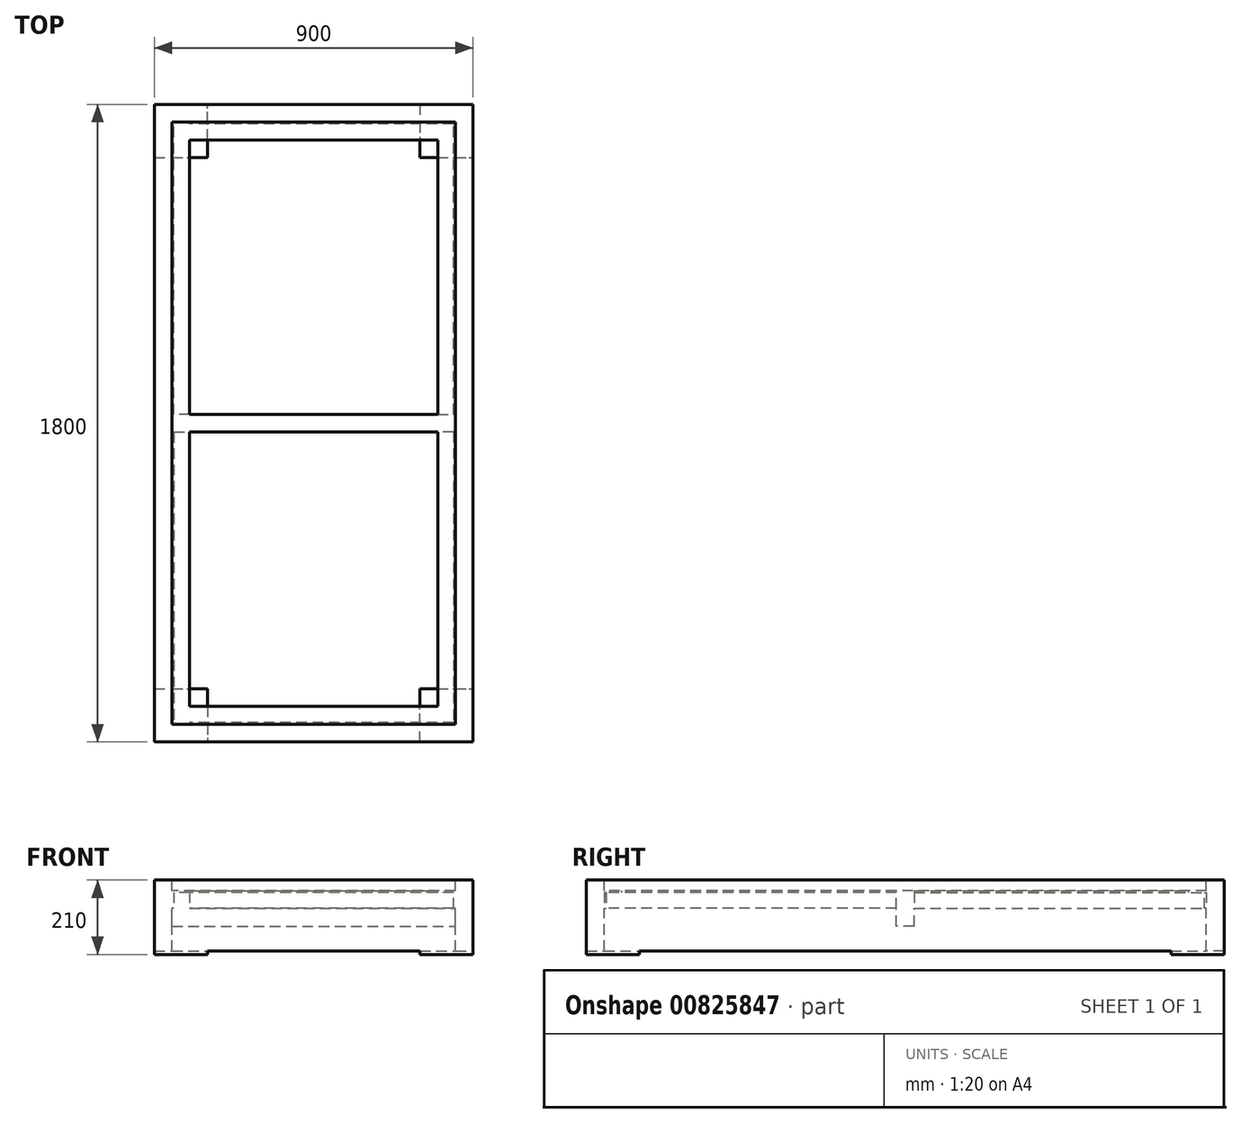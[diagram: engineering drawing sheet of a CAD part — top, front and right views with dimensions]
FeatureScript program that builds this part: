
annotation { "Feature Type Name" : "Feature", "Feature Type Description" : "" }
export const myFeature = defineFeature(function(context is Context, id is Id, definition is map)
    precondition{}
    {
        {
            var Q0;
            Q0=qCreatedBy(makeId("Top.planeOp"),FACE);
            var sketch = newSketch(context, id + "F0", { "sketchPlane" : qUnion([Q0])});
            skLineSegment(sketch, "E0", {"start": v(0, 0) * mm, "end": v(0, 1800) * mm});
            skLineSegment(sketch, "E1", {"start": v(0, 1800) * mm, "end": v(900, 1800) * mm});
            skLineSegment(sketch, "E2", {"start": v(900, 1800) * mm, "end": v(900, 0) * mm});
            skLineSegment(sketch, "E3", {"start": v(900, 0) * mm, "end": v(0, 0) * mm});
            skLineSegment(sketch, "E4.0", {"start": v(50, 50) * mm, "end": v(50, 1750) * mm});
            skLineSegment(sketch, "E5.0", {"start": v(50, 1750) * mm, "end": v(850, 1750) * mm});
            skLineSegment(sketch, "E6.0", {"start": v(850, 1750) * mm, "end": v(850, 50) * mm});
            skLineSegment(sketch, "E7.0", {"start": v(850, 50) * mm, "end": v(50, 50) * mm});
            skLineSegment(sketch, "E8.0", {"start": v(50, 875) * mm, "end": v(850, 875) * mm});
            skLineSegment(sketch, "E9.0", {"start": v(50, 925) * mm, "end": v(850, 925) * mm});
            skPoint(sketch, "E10.end.orphan", {"position": v(850, 900) * mm});
            skPoint(sketch, "E10.start.orphan", {"position": v(50, 900) * mm});
            skSolve(sketch);
        }
        {
            var Q0;
            Q0 = qSketchRegion(id + "F0", true);
            var Q1;
            {var subQ0=sQuery(id+"F0.wireOp",EDGE,"E8.0");Q1=makeQuery(id+"F0.imprint","IMPRINT",FACE,{"disambiguationData":[TD([[makeQuery(id+"F0.imprint","IMPRINT",EDGE,{"derivedFrom":subQ0}),1.0]])]});}
            extrude(context, id + "F1", {"entities" : qUnion([Q0, Q1]), "oppositeDirection" : true, "depth" : 200 * mm, "offsetDistance" : 25 * mm});
        }
        {
            var Q0;
            Q0=makeQuery(id+"F1.opExtrude","SWEPT_FACE",FACE,{"disambiguationData":[OSD([sQuery(id+"F0.wireOp",EDGE,"E8.0")])]});
            var sketch = newSketch(context, id + "F2", { "sketchPlane" : qUnion([Q0])});
            skLineSegment(sketch, "E11", {"start": v(50, 0) * mm, "end": v(50, -30) * mm});
            skLineSegment(sketch, "E12", {"start": v(50, -30) * mm, "end": v(850, -30) * mm});
            skLineSegment(sketch, "E13", {"start": v(850, -30) * mm, "end": v(850, 0) * mm});
            skLineSegment(sketch, "E14", {"start": v(850, 0) * mm, "end": v(50, 0) * mm});
            skSolve(sketch);
        }
        {
            var Q0;
            Q0 = qSketchRegion(id + "F2", true);
            extrude(context, id + "F3", {"entities" : qUnion([Q0]), "operationType" : NewBodyOperationType.REMOVE, "endBound" : BoundingType.UP_TO_NEXT, "oppositeDirection" : true, "depth" : 25 * mm, "offsetDistance" : 25 * mm});
        }
        {
            var Q0;
            Q0=makeQuery(id+"F1.opExtrude","SWEPT_FACE",FACE,{"disambiguationData":[OSD([sQuery(id+"F0.wireOp",EDGE,"E8.0")])]});
            var sketch = newSketch(context, id + "F4", { "sketchPlane" : qUnion([Q0])});
            skLineSegment(sketch, "E15", {"start": v(50, -200) * mm, "end": v(50, -130) * mm});
            skLineSegment(sketch, "E16", {"start": v(50, -130) * mm, "end": v(850, -130) * mm});
            skLineSegment(sketch, "E17", {"start": v(850, -130) * mm, "end": v(850, -200) * mm});
            skLineSegment(sketch, "E18", {"start": v(850, -200) * mm, "end": v(50, -200) * mm});
            skSolve(sketch);
        }
        {
            var Q0;
            Q0 = qSketchRegion(id + "F4", true);
            extrude(context, id + "F5", {"entities" : qUnion([Q0]), "operationType" : NewBodyOperationType.REMOVE, "endBound" : BoundingType.UP_TO_NEXT, "oppositeDirection" : true, "depth" : 25 * mm, "offsetDistance" : 25 * mm});
        }
        {
            var Q0;
            Q0=makeQuery(id+"F1.opExtrude","CAP_FACE",FACE,{"disambiguationData":[OSD([sQuery(id+"F0.wireOp",EDGE,"E0"),sQuery(id+"F0.wireOp",EDGE,"E1"),sQuery(id+"F0.wireOp",EDGE,"E2"),sQuery(id+"F0.wireOp",EDGE,"E3"),sQuery(id+"F0.wireOp",EDGE,"E4.0"),sQuery(id+"F0.wireOp",EDGE,"E5.0"),sQuery(id+"F0.wireOp",EDGE,"E6.0"),sQuery(id+"F0.wireOp",EDGE,"E7.0"),sQuery(id+"F0.wireOp",EDGE,"E8.0"),sQuery(id+"F0.wireOp",EDGE,"E9.0")])],"isStart":false});
            var sketch = newSketch(context, id + "F6", { "sketchPlane" : qUnion([Q0])});
            skLineSegment(sketch, "E19", {"start": v(0, 0) * mm, "end": v(0, -150) * mm});
            skLineSegment(sketch, "E20", {"start": v(0, -150) * mm, "end": v(150, -150) * mm});
            skLineSegment(sketch, "E21", {"start": v(150, -150) * mm, "end": v(150, 0) * mm});
            skLineSegment(sketch, "E22", {"start": v(150, 0) * mm, "end": v(0, 0) * mm});
            skLineSegment(sketch, "E23", {"start": v(900, 0) * mm, "end": v(750, 0) * mm});
            skLineSegment(sketch, "E24", {"start": v(750, 0) * mm, "end": v(750, -150) * mm});
            skLineSegment(sketch, "E25", {"start": v(750, -150) * mm, "end": v(900, -150) * mm});
            skLineSegment(sketch, "E26", {"start": v(900, -150) * mm, "end": v(900, 0) * mm});
            skLineSegment(sketch, "E27", {"start": v(0, -1800) * mm, "end": v(0, -1650) * mm});
            skLineSegment(sketch, "E28", {"start": v(0, -1650) * mm, "end": v(150, -1650) * mm});
            skLineSegment(sketch, "E29", {"start": v(150, -1650) * mm, "end": v(150, -1800) * mm});
            skLineSegment(sketch, "E30", {"start": v(150, -1800) * mm, "end": v(0, -1800) * mm});
            skLineSegment(sketch, "E31", {"start": v(900, -1800) * mm, "end": v(750, -1800) * mm});
            skLineSegment(sketch, "E32", {"start": v(750, -1800) * mm, "end": v(750, -1650) * mm});
            skLineSegment(sketch, "E33", {"start": v(750, -1650) * mm, "end": v(900, -1650) * mm});
            skLineSegment(sketch, "E34", {"start": v(900, -1650) * mm, "end": v(900, -1800) * mm});
            skSolve(sketch);
        }
        {
            var Q0;
            Q0 = qSketchRegion(id + "F6", true);
            extrude(context, id + "F7", {"entities" : qUnion([Q0]), "operationType" : NewBodyOperationType.ADD, "depth" : 10 * mm, "offsetDistance" : 25 * mm});
        }
        {
            var Q0;
            Q0=makeQuery(id+"F1.opExtrude","SWEPT_FACE",FACE,{"disambiguationData":[OSD([sQuery(id+"F0.wireOp",EDGE,"E5.0")])]});
            var sketch = newSketch(context, id + "F8", { "sketchPlane" : qUnion([Q0])});
            skLineSegment(sketch, "E35", {"start": v(50, -30) * mm, "end": v(100, -30) * mm});
            skLineSegment(sketch, "E36", {"start": v(100, -30) * mm, "end": v(100, -35) * mm});
            skLineSegment(sketch, "E37", {"start": v(100, -35) * mm, "end": v(55, -35) * mm});
            skLineSegment(sketch, "E38", {"start": v(55, -35) * mm, "end": v(55, -80) * mm});
            skLineSegment(sketch, "E39", {"start": v(55, -80) * mm, "end": v(50, -80) * mm});
            skLineSegment(sketch, "E40", {"start": v(50, -80) * mm, "end": v(50, -30) * mm});
            skLineSegment(sketch, "E41", {"start": v(450, 0) * mm, "end": v(450, -200) * mm, "construction": true});
            skLineSegment(sketch, "E42.MirrorCS", {"start": v(845, -80) * mm, "end": v(850, -80) * mm});
            skLineSegment(sketch, "E43.MirrorCS", {"start": v(800, -30) * mm, "end": v(800, -35) * mm});
            skLineSegment(sketch, "E44.MirrorCS", {"start": v(800, -35) * mm, "end": v(845, -35) * mm});
            skLineSegment(sketch, "E45.MirrorCS", {"start": v(850, -30) * mm, "end": v(800, -30) * mm});
            skLineSegment(sketch, "E46.MirrorCS", {"start": v(850, -80) * mm, "end": v(850, -30) * mm});
            skLineSegment(sketch, "E47.MirrorCS", {"start": v(845, -35) * mm, "end": v(845, -80) * mm});
            skSolve(sketch);
        }
        {
            var Q0;
            Q0 = qSketchRegion(id + "F8", true);
            extrude(context, id + "F9", {"entities" : qUnion([Q0]), "operationType" : NewBodyOperationType.ADD, "endBound" : BoundingType.UP_TO_NEXT, "depth" : 25 * mm, "offsetDistance" : 25 * mm});
        }
        {
            var Q0;
            Q0=makeQuery(id+"F1.opExtrude","SWEPT_FACE",FACE,{"disambiguationData":[OSD([sQuery(id+"F0.wireOp",EDGE,"E7.0")])]});
            var sketch = newSketch(context, id + "F10", { "sketchPlane" : qUnion([Q0])});
            skLineSegment(sketch, "E48", {"start": v(-850, -30) * mm, "end": v(-800, -30) * mm});
            skLineSegment(sketch, "E49", {"start": v(-800, -30) * mm, "end": v(-800, -35) * mm});
            skLineSegment(sketch, "E50", {"start": v(-800, -35) * mm, "end": v(-845, -35) * mm});
            skLineSegment(sketch, "E51", {"start": v(-845, -35) * mm, "end": v(-845, -80) * mm});
            skLineSegment(sketch, "E52", {"start": v(-845, -80) * mm, "end": v(-850, -80) * mm});
            skLineSegment(sketch, "E53", {"start": v(-850, -80) * mm, "end": v(-850, -30) * mm});
            skLineSegment(sketch, "E54", {"start": v(-450, 0) * mm, "end": v(-450, -219.64) * mm, "construction": true});
            skLineSegment(sketch, "E55.MirrorCS", {"start": v(-55, -80) * mm, "end": v(-50, -80) * mm});
            skLineSegment(sketch, "E56.MirrorCS", {"start": v(-100, -30) * mm, "end": v(-100, -35) * mm});
            skLineSegment(sketch, "E57.MirrorCS", {"start": v(-100, -35) * mm, "end": v(-55, -35) * mm});
            skLineSegment(sketch, "E58.MirrorCS", {"start": v(-50, -30) * mm, "end": v(-100, -30) * mm});
            skLineSegment(sketch, "E59.MirrorCS", {"start": v(-50, -80) * mm, "end": v(-50, -30) * mm});
            skLineSegment(sketch, "E60.MirrorCS", {"start": v(-55, -35) * mm, "end": v(-55, -80) * mm});
            skLineSegment(sketch, "E61", {"start": v(-850, 0) * mm, "end": v(-850, -30) * mm, "construction": true});
            skSolve(sketch);
        }
        {
            var Q0;
            Q0 = qSketchRegion(id + "F10", true);
            extrude(context, id + "F11", {"entities" : qUnion([Q0]), "operationType" : NewBodyOperationType.ADD, "endBound" : BoundingType.UP_TO_NEXT, "depth" : 25 * mm, "offsetDistance" : 25 * mm});
        }
        {
            var Q0;
            Q0=makeQuery(id+"F11.opExtrude","SWEPT_FACE",FACE,{"disambiguationData":[OSD([sQuery(id+"F10.wireOp",EDGE,"E56.MirrorCS")])]});
            var sketch = newSketch(context, id + "F12", { "sketchPlane" : qUnion([Q0])});
            skLineSegment(sketch, "E62", {"start": v(50, -30) * mm, "end": v(50, -80) * mm});
            skLineSegment(sketch, "E63", {"start": v(50, -80) * mm, "end": v(55, -80) * mm});
            skLineSegment(sketch, "E64", {"start": v(55, -80) * mm, "end": v(55, -35) * mm});
            skLineSegment(sketch, "E65", {"start": v(55, -35) * mm, "end": v(100, -35) * mm});
            skLineSegment(sketch, "E66", {"start": v(100, -35) * mm, "end": v(100, -30) * mm});
            skLineSegment(sketch, "E67", {"start": v(100, -30) * mm, "end": v(50, -30) * mm});
            skSolve(sketch);
        }
        {
            var Q0;
            Q0 = qSketchRegion(id + "F12", true);
            extrude(context, id + "F13", {"entities" : qUnion([Q0]), "operationType" : NewBodyOperationType.ADD, "endBound" : BoundingType.UP_TO_NEXT, "depth" : 25 * mm, "offsetDistance" : 25 * mm});
        }
        {
            var Q0;
            Q0=makeQuery(id+"F9.opExtrude","SWEPT_FACE",FACE,{"disambiguationData":[OSD([sQuery(id+"F8.wireOp",EDGE,"E36")])]});
            var sketch = newSketch(context, id + "F14", { "sketchPlane" : qUnion([Q0])});
            skLineSegment(sketch, "E68", {"start": v(1750, -30) * mm, "end": v(1750, -80) * mm});
            skLineSegment(sketch, "E69", {"start": v(1750, -80) * mm, "end": v(1745, -80) * mm});
            skLineSegment(sketch, "E70", {"start": v(1745, -80) * mm, "end": v(1745, -35) * mm});
            skLineSegment(sketch, "E71", {"start": v(1745, -35) * mm, "end": v(1700, -35) * mm});
            skLineSegment(sketch, "E72", {"start": v(1700, -35) * mm, "end": v(1700, -30) * mm});
            skLineSegment(sketch, "E73", {"start": v(1700, -30) * mm, "end": v(1750, -30) * mm});
            skSolve(sketch);
        }
        {
            var Q0;
            Q0 = qSketchRegion(id + "F14", true);
            extrude(context, id + "F15", {"entities" : qUnion([Q0]), "operationType" : NewBodyOperationType.ADD, "endBound" : BoundingType.UP_TO_NEXT, "depth" : 25 * mm, "offsetDistance" : 25 * mm});
        }
    });
